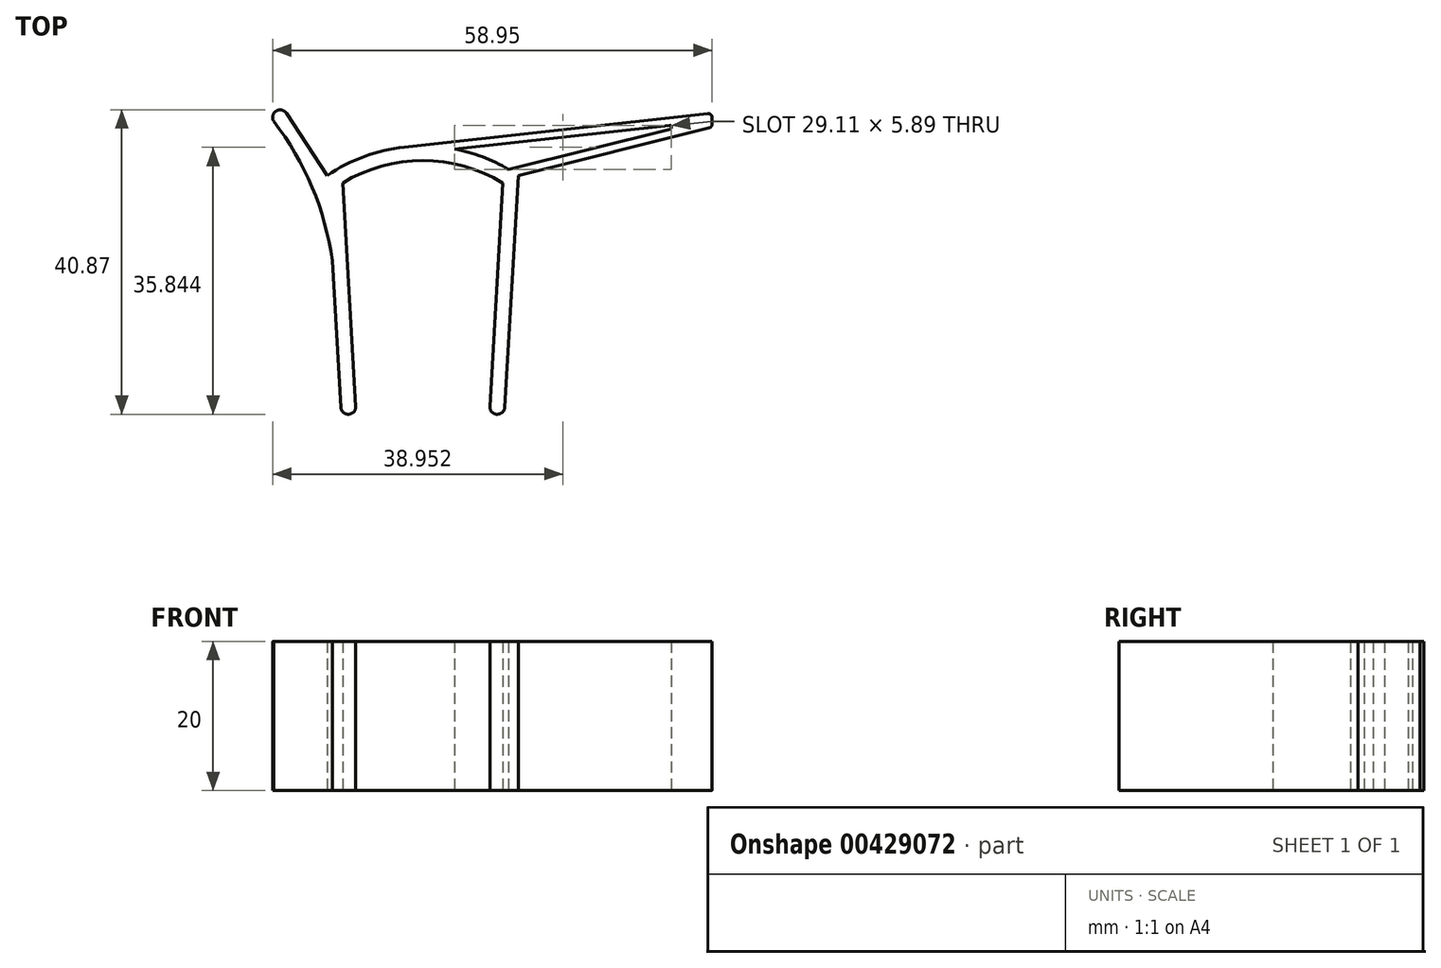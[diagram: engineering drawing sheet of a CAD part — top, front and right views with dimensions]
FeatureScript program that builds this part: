
annotation { "Feature Type Name" : "Feature", "Feature Type Description" : "" }
export const myFeature = defineFeature(function(context is Context, id is Id, definition is map)
    precondition{}
    {
        {
            var Q0;
            Q0=qCreatedBy(makeId("Top.planeOp"),FACE);
            var sketch = newSketch(context, id + "F0", { "sketchPlane" : qUnion([Q0])});
            skLineSegment(sketch, "E0", {"start": v(-10.16, 3.4) * mm, "end": v(11.34, 3.4) * mm, "construction": true});
            skArc(sketch, "E1", {"start": v(11.34, 3.4) * mm, "mid": v(0.59, 6.4) * mm, "end": v(-10.16, 3.4) * mm});
            skLineSegment(sketch, "E2", {"start": v(0.59, 3.4) * mm, "end": v(0.59, -26.6) * mm, "construction": true});
            skLineSegment(sketch, "E3", {"start": v(-8.41, -26.6) * mm, "end": v(9.59, -26.6) * mm, "construction": true});
            skLineSegment(sketch, "E4", {"start": v(-10.16, 3.4) * mm, "end": v(-8.41, -26.6) * mm});
            skLineSegment(sketch, "E5", {"start": v(11.34, 3.4) * mm, "end": v(9.59, -26.6) * mm});
            skLineSegment(sketch, "E6", {"start": v(-8.41, -26.6) * mm, "end": v(-10.4, -26.72) * mm});
            skLineSegment(sketch, "E7", {"start": v(9.59, -26.6) * mm, "end": v(11.59, -26.72) * mm});
            skLineSegment(sketch, "E8", {"start": v(-10.4, -26.72) * mm, "end": v(-12.22, 4.4) * mm});
            skLineSegment(sketch, "E9", {"start": v(11.59, -26.72) * mm, "end": v(13.4, 4.4) * mm});
            skArc(sketch, "E10", {"start": v(13.4, 4.4) * mm, "mid": v(0.59, 8.36) * mm, "end": v(-12.22, 4.4) * mm});
            skLineSegment(sketch, "E11", {"start": v(-12.22, 4.4) * mm, "end": v(-17.72, 12.76) * mm});
            skLineSegment(sketch, "E12", {"start": v(-17.72, 12.76) * mm, "end": v(-19.4, 11.66) * mm});
            skArc(sketch, "E13", {"start": v(-11.56, -7.04) * mm, "mid": v(-14.25, 2.82) * mm, "end": v(-19.4, 11.66) * mm});
            skArc(sketch, "E14", {"start": v(-17.72, 12.76) * mm, "mid": v(-19.1, 13.05) * mm, "end": v(-19.4, 11.66) * mm});
            skArc(sketch, "E15", {"start": v(-10.4, -26.72) * mm, "mid": v(-9.35, -27.66) * mm, "end": v(-8.41, -26.6) * mm});
            skArc(sketch, "E16", {"start": v(9.59, -26.6) * mm, "mid": v(10.53, -27.66) * mm, "end": v(11.59, -26.72) * mm});
            skLineSegment(sketch, "E17", {"start": v(13.4, 4.4) * mm, "end": v(39.4, 4.4) * mm, "construction": true});
            skLineSegment(sketch, "E18", {"start": v(39.4, 4.4) * mm, "end": v(39.4, 23.4) * mm, "construction": true});
            skLineSegment(sketch, "E19", {"start": v(-1.9, 8.23) * mm, "end": v(38.85, 12.7) * mm});
            skLineSegment(sketch, "E20", {"start": v(13.4, 4.4) * mm, "end": v(39.02, 10.79) * mm});
            skLineSegment(sketch, "E21", {"start": v(39.4, 11.27) * mm, "end": v(39.4, 12.2) * mm});
            skPoint(sketch, "E22.visualSharp", {"position": v(39.4, 12.76) * mm});
            skArc(sketch, "E22.filletArc", {"start": v(39.4, 12.2) * mm, "mid": v(39.23, 12.58) * mm, "end": v(38.85, 12.7) * mm});
            skPoint(sketch, "E23.visualSharp", {"position": v(39.4, 10.88) * mm});
            skArc(sketch, "E23.filletArc", {"start": v(39.02, 10.79) * mm, "mid": v(39.3, 10.96) * mm, "end": v(39.4, 11.27) * mm});
            skLineSegment(sketch, "E24", {"start": v(4.85, 7.96) * mm, "end": v(33.68, 11.13) * mm});
            skLineSegment(sketch, "E25", {"start": v(33.77, 10.64) * mm, "end": v(12.09, 5.24) * mm});
            skPoint(sketch, "E26.visualSharp", {"position": v(37.37, 11.53) * mm});
            skArc(sketch, "E26.filletArc", {"start": v(33.77, 10.64) * mm, "mid": v(33.96, 10.92) * mm, "end": v(33.68, 11.13) * mm});
            skSolve(sketch);
        }
        {
            var Q0;
            Q0=makeQuery(id+"F0.imprint","IMPRINT",FACE,{"disambiguationData":[TD([[makeQuery(id+"F0.imprint","IMPRINT",EDGE,{"derivedFrom":sQuery(id+"F0.wireOp",EDGE,"E6")}),1.0]])]});
            var Q1;
            Q1=makeQuery(id+"F0.imprint","IMPRINT",FACE,{"disambiguationData":[TD([[makeQuery(id+"F0.imprint","IMPRINT",EDGE,{"derivedFrom":sQuery(id+"F0.wireOp",EDGE,"E7")}),-1.0]])]});
            var Q2;
            Q2=makeQuery(id+"F0.imprint","IMPRINT",FACE,{"disambiguationData":[TD([[makeQuery(id+"F0.imprint","IMPRINT",EDGE,{"derivedFrom":sQuery(id+"F0.wireOp",EDGE,"E1")}),-1.0]])]});
            var Q3;
            {var subQ0=sQuery(id+"F0.wireOp",EDGE,"E11");Q3=makeQuery(id+"F0.imprint","IMPRINT",FACE,{"disambiguationData":[TD([[makeQuery(id+"F0.imprint","IMPRINT",EDGE,{"derivedFrom":subQ0}),1.0]])]});}
            var Q4;
            Q4=makeQuery(id+"F0.imprint","IMPRINT",FACE,{"disambiguationData":[TD([[makeQuery(id+"F0.imprint","IMPRINT",EDGE,{"derivedFrom":sQuery(id+"F0.wireOp",EDGE,"E12")}),-1.0]])]});
            var Q5;
            {var subQ3=sQuery(id+"F0.wireOp",EDGE,"E19");Q5=makeQuery(id+"F0.imprint","IMPRINT",FACE,{"disambiguationData":[TD([[makeQuery(id+"F0.imprint","IMPRINT",EDGE,{"derivedFrom":subQ3}),-1.0]])]});}
            extrude(context, id + "F1", {"entities" : qUnion([Q0, Q1, Q2, Q3, Q4, Q5]), "depth" : 20 * mm});
        }
    });
